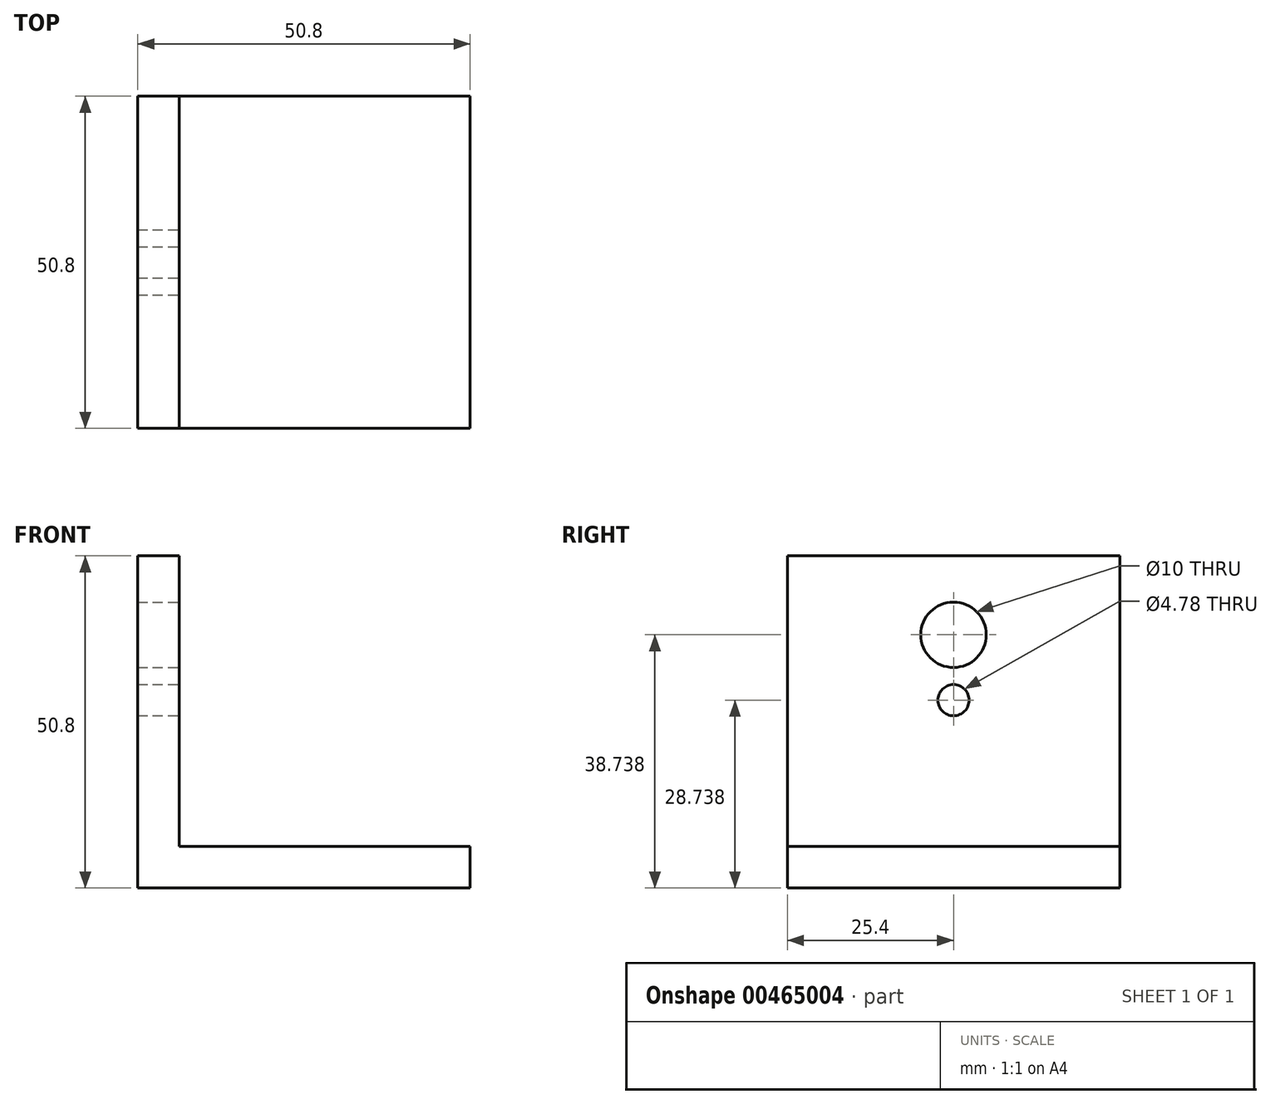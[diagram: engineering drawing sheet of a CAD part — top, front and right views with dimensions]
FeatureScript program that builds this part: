
annotation { "Feature Type Name" : "Feature", "Feature Type Description" : "" }
export const myFeature = defineFeature(function(context is Context, id is Id, definition is map)
    precondition{}
    {
        {
            var Q0;
            Q0=qCreatedBy(makeId("Front.planeOp"),FACE);
            var sketch = newSketch(context, id + "F0", { "sketchPlane" : qUnion([Q0])});
            skLineSegment(sketch, "E0", {"start": v(0, 0) * mm, "end": v(0, 50.8) * mm});
            skLineSegment(sketch, "E1", {"start": v(0, 50.8) * mm, "end": v(6.35, 50.8) * mm});
            skLineSegment(sketch, "E2", {"start": v(6.35, 50.8) * mm, "end": v(6.35, 6.35) * mm});
            skLineSegment(sketch, "E3", {"start": v(6.35, 6.35) * mm, "end": v(50.8, 6.35) * mm});
            skLineSegment(sketch, "E4", {"start": v(50.8, 6.35) * mm, "end": v(50.8, 0) * mm});
            skLineSegment(sketch, "E5", {"start": v(50.8, 0) * mm, "end": v(0, 0) * mm});
            skSolve(sketch);
        }
        {
            var Q0;
            Q0=makeQuery(id+"F0.imprint","IMPRINT",FACE,{"disambiguationData":[TD([[makeQuery(id+"F0.imprint","IMPRINT",EDGE,{"derivedFrom":sQuery(id+"F0.wireOp",EDGE,"E0")}),-1.0]])]});
            extrude(context, id + "F1", {"entities" : qUnion([Q0]), "depth" : 50.8 * mm});
        }
        {
            var Q0;
            Q0=makeQuery(id+"F1.opExtrude","SWEPT_FACE",FACE,{"disambiguationData":[OSD([sQuery(id+"F0.wireOp",EDGE,"E2")])]});
            var sketch = newSketch(context, id + "F2", { "sketchPlane" : qUnion([Q0])});
            skLineSegment(sketch, "E6", {"start": v(-25.4, 50.8) * mm, "end": v(-25.4, 6.35) * mm, "construction": true});
            skCircle(sketch, "E7", {"center": v(-25.4, 38.74) * mm, "radius": 5 * mm});
            skSolve(sketch);
        }
        {
            var Q0;
            Q0 = qSketchRegion(id + "F2", true);
            extrude(context, id + "F3", {"entities" : qUnion([Q0]), "operationType" : NewBodyOperationType.REMOVE, "endBound" : BoundingType.THROUGH_ALL, "oppositeDirection" : true, "depth" : 25 * mm});
        }
        {
            var Q0;
            Q0=makeQuery(id+"F1.opExtrude","SWEPT_FACE",FACE,{"disambiguationData":[OSD([sQuery(id+"F0.wireOp",EDGE,"E2")])]});
            var sketch = newSketch(context, id + "F4", { "sketchPlane" : qUnion([Q0])});
            skLineSegment(sketch, "E8", {"start": v(-25.4, 38.74) * mm, "end": v(-25.4, 0) * mm, "construction": true});
            skLineSegment(sketch, "E9", {"start": v(-25.4, 38.74) * mm, "end": v(-4.22, 38.74) * mm, "construction": true});
            skPoint(sketch, "E10", {"position": v(-25.4, 28.74) * mm});
            skSolve(sketch);
        }
        {
            var Q0;
            Q0=sQuery(id+"F4.wireOp",VERTEX,"E10");
            var Q1;
            Q1=makeQuery(id+"F1.opExtrude","SWEPT_BODY",BODY,{"disambiguationData":[OSD([sQuery(id+"F0.wireOp",EDGE,"E0"),sQuery(id+"F0.wireOp",EDGE,"E1"),sQuery(id+"F0.wireOp",EDGE,"E2"),sQuery(id+"F0.wireOp",EDGE,"E3"),sQuery(id+"F0.wireOp",EDGE,"E4"),sQuery(id+"F0.wireOp",EDGE,"E5")])]});
            hole(context, id + "F5", {"style" : HoleStyle.SIMPLE, "endStyle" : HoleEndStyle.THROUGH, "holeDiameter" : 4.78 * mm, "majorDiameter" : 5 * mm, "isTappedThrough" : true, "tappedDepth" : 12 * mm, "tapClearance" : 3, "locations" : qUnion([Q0]), "scope" : qUnion([Q1])});
        }
    });
